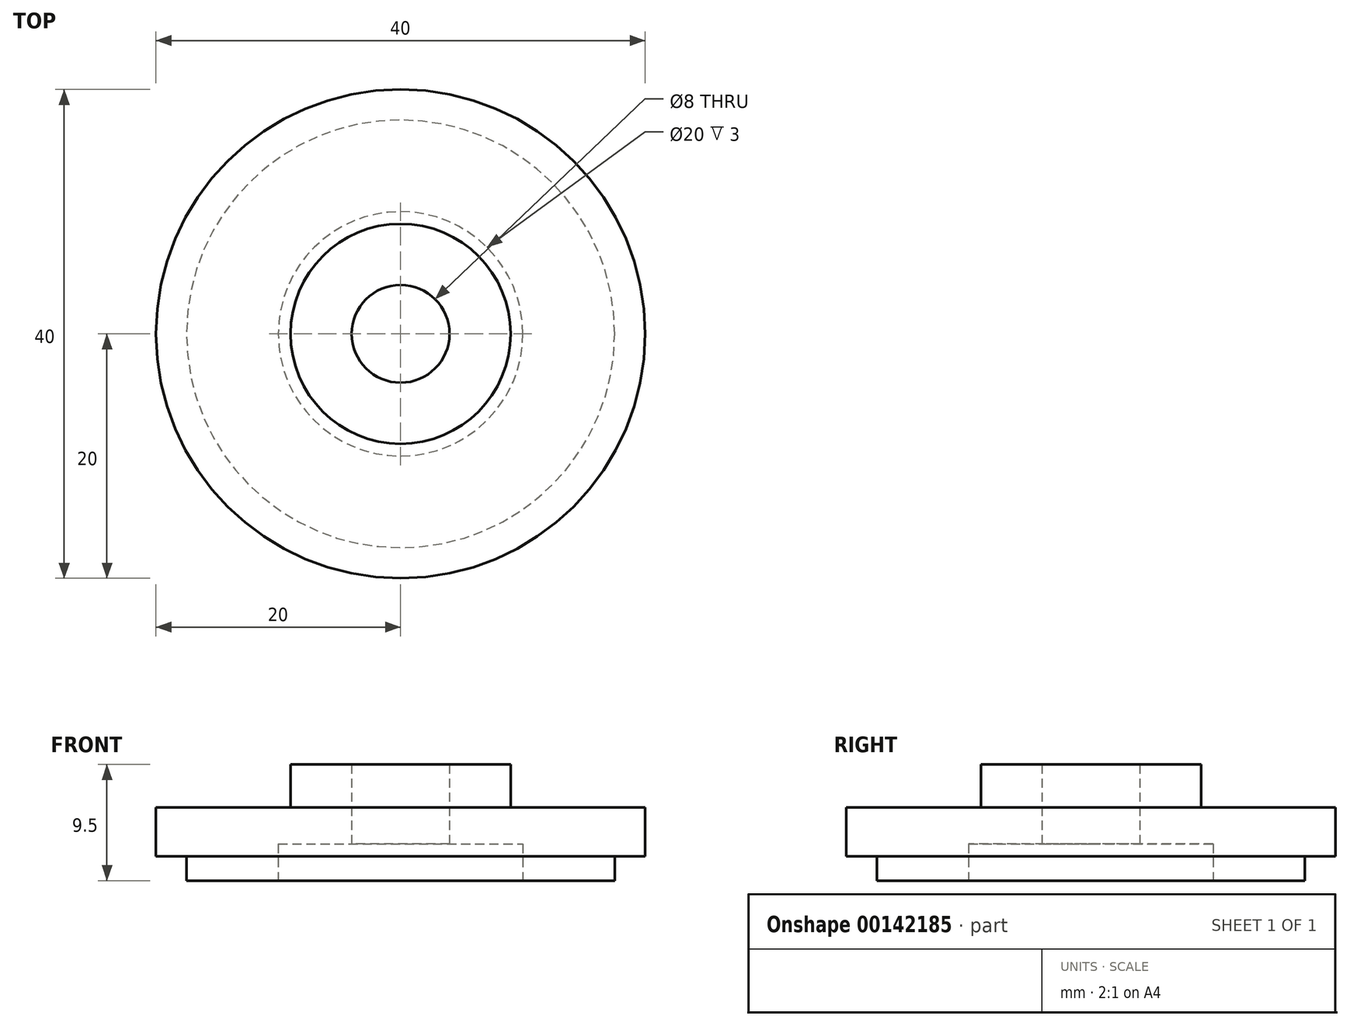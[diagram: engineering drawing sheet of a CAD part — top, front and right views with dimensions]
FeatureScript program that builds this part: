
annotation { "Feature Type Name" : "Feature", "Feature Type Description" : "" }
export const myFeature = defineFeature(function(context is Context, id is Id, definition is map)
    precondition{}
    {
        {
            var Q0;
            Q0=qCreatedBy(makeId("Top.planeOp"),FACE);
            var sketch = newSketch(context, id + "F0", { "sketchPlane" : qUnion([Q0])});
            skCircle(sketch, "E0", {"center": v(0, 0) * mm, "radius": 20 * mm});
            skCircle(sketch, "E1", {"center": v(0, 0) * mm, "radius": 9 * mm});
            skCircle(sketch, "E2", {"center": v(0, 0) * mm, "radius": 4 * mm});
            skSolve(sketch);
        }
        {
            var Q0;
            Q0=makeQuery(id+"F0.imprint","IMPRINT",FACE,{"disambiguationData":[TD([[makeQuery(id+"F0.imprint","IMPRINT",EDGE,{"derivedFrom":sQuery(id+"F0.wireOp",EDGE,"E1")}),1.0]])]});
            extrude(context, id + "F1", {"entities" : qUnion([Q0]), "depth" : 3.5 * mm});
        }
        {
            var Q0;
            Q0=makeQuery(id+"F0.imprint","IMPRINT",FACE,{"disambiguationData":[TD([[makeQuery(id+"F0.imprint","IMPRINT",EDGE,{"derivedFrom":sQuery(id+"F0.wireOp",EDGE,"E0")}),1.0]])]});
            var Q1;
            Q1=makeQuery(id+"F0.imprint","IMPRINT",FACE,{"disambiguationData":[TD([[makeQuery(id+"F0.imprint","IMPRINT",EDGE,{"derivedFrom":sQuery(id+"F0.wireOp",EDGE,"E1")}),1.0]])]});
            extrude(context, id + "F2", {"entities" : qUnion([Q0, Q1]), "operationType" : NewBodyOperationType.ADD, "oppositeDirection" : true, "depth" : 6 * mm});
        }
        {
            var Q0;
            Q0=makeQuery(id+"F2.opExtrude","CAP_FACE",FACE,{"disambiguationData":[OSD([sQuery(id+"F0.wireOp",EDGE,"E0"),sQuery(id+"F0.wireOp",EDGE,"E2")])],"isStart":false});
            var sketch = newSketch(context, id + "F3", { "sketchPlane" : qUnion([Q0])});
            skCircle(sketch, "E3", {"center": v(0, 0) * mm, "radius": 10 * mm});
            skCircle(sketch, "E4", {"center": v(0, 0) * mm, "radius": 17.5 * mm});
            skSolve(sketch);
        }
        {
            var Q0;
            Q0=makeQuery(id+"F3.imprint","IMPRINT",FACE,{"disambiguationData":[TD([[makeQuery(id+"F3.imprint","IMPRINT",EDGE,{"derivedFrom":sQuery(id+"F3.wireOp",EDGE,"E3")}),1.0]])]});
            extrude(context, id + "F4", {"entities" : qUnion([Q0]), "operationType" : NewBodyOperationType.REMOVE, "oppositeDirection" : true, "depth" : 3 * mm});
        }
        {
            var Q0;
            Q0=makeQuery(id+"F3.imprint","IMPRINT",FACE,{"disambiguationData":[TD([[makeQuery(id+"F3.imprint","IMPRINT",EDGE,{"derivedFrom":sQuery(id+"F3.wireOp",EDGE,"E4")}),-1.0]])]});
            extrude(context, id + "F5", {"entities" : qUnion([Q0]), "operationType" : NewBodyOperationType.REMOVE, "oppositeDirection" : true, "depth" : 2 * mm});
        }
    });
